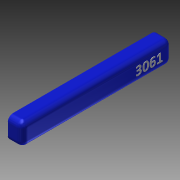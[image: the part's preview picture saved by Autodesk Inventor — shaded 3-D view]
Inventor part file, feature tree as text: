
AUTODESK INVENTOR PART (.ipt)
format: ipt  version: 2013 (Build 170138000, 138)  size: 364,544 bytes
history: native  units: in
note: dims shown in document units (in); Inventor stores cm internally (conversion verified against a paired STEP export)
features: reference x7, extrude x4, sketch x3, fillet x1, projected_geometry x1
ambient origin geometry x8: Origin, YZ Plane, XZ Plane, XY Plane, X Axis, Y Axis, Z Axis, Center Point
bodies: Solid1 (feature_tree)
feature tree (16):
  sketch  "Sketch1"  dims[d0=0.0625in d1=0.0in d3=1.0in]
  extrude  "Extrusion1"  Depth=1.0in
  extrude  "Extrusion2"  Depth=0.0625in
  extrude  "Extrusion3"  Depth=0.0625in TaperAngle=0.0deg
  fillet  "Fillet1"  Radius=1.3125in
  extrude  "Extrusion5"  Depth=0.0625in
  reference  "Reference4"
  reference  "Reference5"
  sketch  "Sketch2"  dims[d7=1.0in d9=0.0625in]
  reference  "Reference6"
  reference  "Reference7"
  reference  "Reference8"
  reference  "Reference9"
  reference  "Reference10"
  projected_geometry  "Projected Loop1"
  sketch  "Sketch4"  dims[d10=34.5in d11=0.0in d12=0.0625in d13=0.0in d14=1.3125in d20=0.0625in d21=0.0625in d26=1.0in d27=6.0in d28=2.5in d29=0.0625in d30=0.0in]
